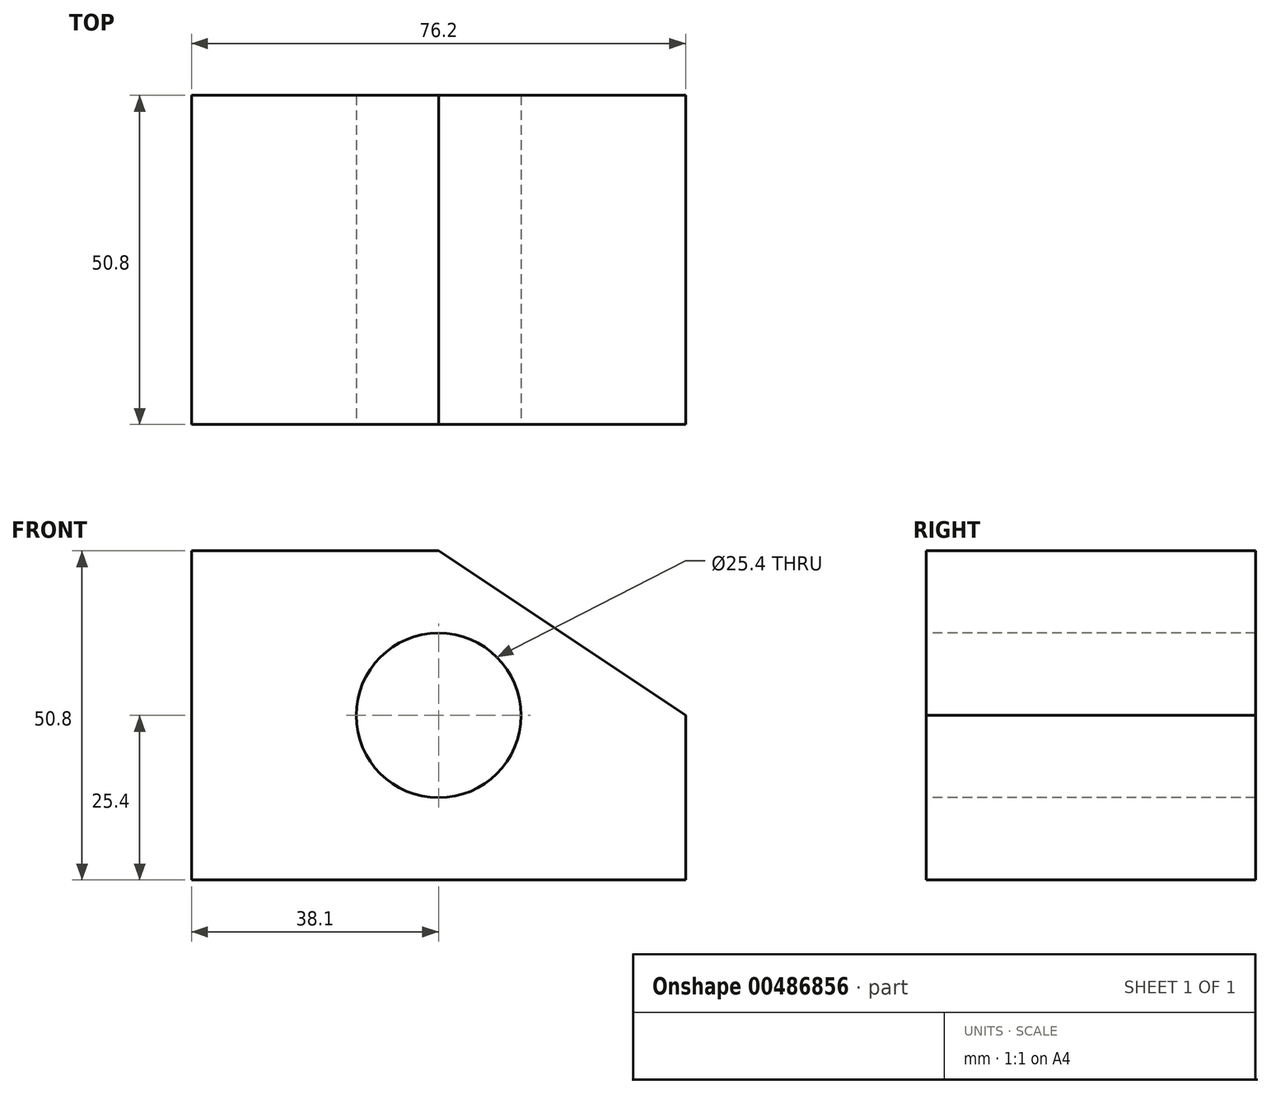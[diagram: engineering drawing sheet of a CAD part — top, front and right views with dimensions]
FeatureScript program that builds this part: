
annotation { "Feature Type Name" : "Feature", "Feature Type Description" : "" }
export const myFeature = defineFeature(function(context is Context, id is Id, definition is map)
    precondition{}
    {
        {
            var Q0;
            Q0=qCreatedBy(makeId("Front.planeOp"),FACE);
            var sketch = newSketch(context, id + "F0", { "sketchPlane" : qUnion([Q0])});
            skLineSegment(sketch, "E0.bottom", {"start": v(0, 0) * mm, "end": v(38.1, 0) * mm});
            skLineSegment(sketch, "E0.top", {"start": v(0, 50.8) * mm, "end": v(38.1, 50.8) * mm});
            skLineSegment(sketch, "E0.left", {"start": v(0, 0) * mm, "end": v(0, 50.8) * mm});
            skLineSegment(sketch, "E1.bottom", {"start": v(38.1, 0) * mm, "end": v(76.2, 0) * mm});
            skLineSegment(sketch, "E1.right", {"start": v(76.2, 0) * mm, "end": v(76.2, 25.4) * mm});
            skLineSegment(sketch, "E2", {"start": v(76.2, 25.4) * mm, "end": v(38.1, 50.8) * mm});
            skCircle(sketch, "E3", {"center": v(38.1, 25.4) * mm, "radius": 12.7 * mm});
            skSolve(sketch);
        }
        {
            var Q0;
            Q0 = qSketchRegion(id + "F0", true);
            extrude(context, id + "F1", {"entities" : qUnion([Q0]), "oppositeDirection" : true, "depth" : 50.8 * mm});
        }
    });
